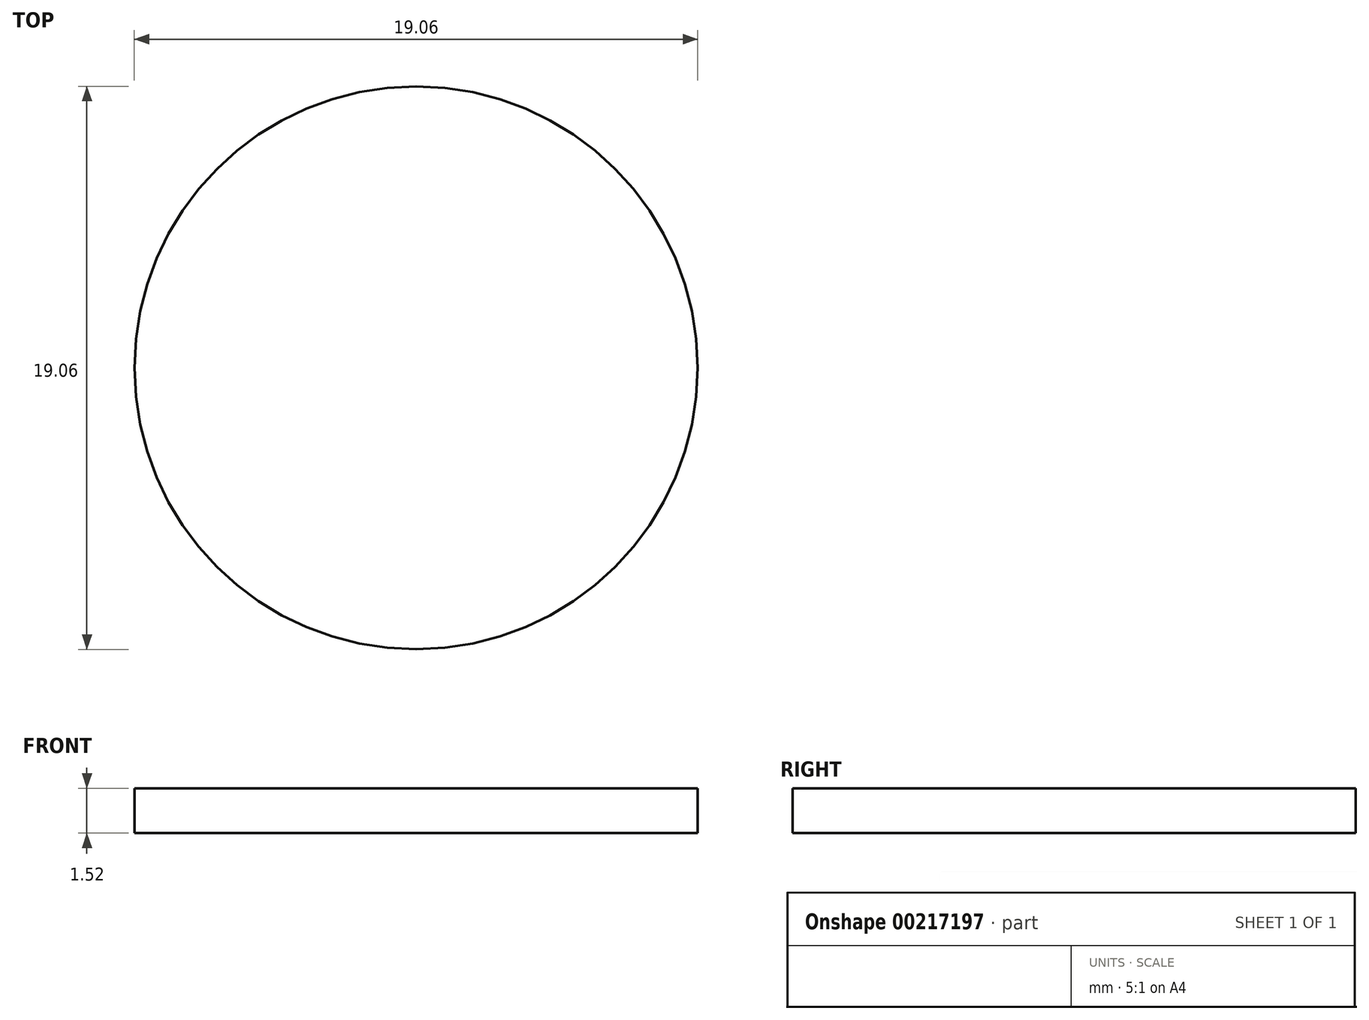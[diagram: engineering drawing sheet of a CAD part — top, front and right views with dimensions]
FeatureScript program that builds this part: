
annotation { "Feature Type Name" : "Feature", "Feature Type Description" : "" }
export const myFeature = defineFeature(function(context is Context, id is Id, definition is map)
    precondition{}
    {
        {
            var Q0;
            Q0=qCreatedBy(makeId("Top.planeOp"),FACE);
            var sketch = newSketch(context, id + "F0", { "sketchPlane" : qUnion([Q0])});
            skCircle(sketch, "E0", {"center": v(0, 0) * mm, "radius": 9.53 * mm});
            skSolve(sketch);
        }
        {
            var Q0;
            Q0=qSketchRegion(id+"F0",true);
            extrude(context, id + "F1", {"entities" : qUnion([Q0]), "endBound" : BoundingType.SYMMETRIC, "depth" : 1.52 * mm});
        }
    });
